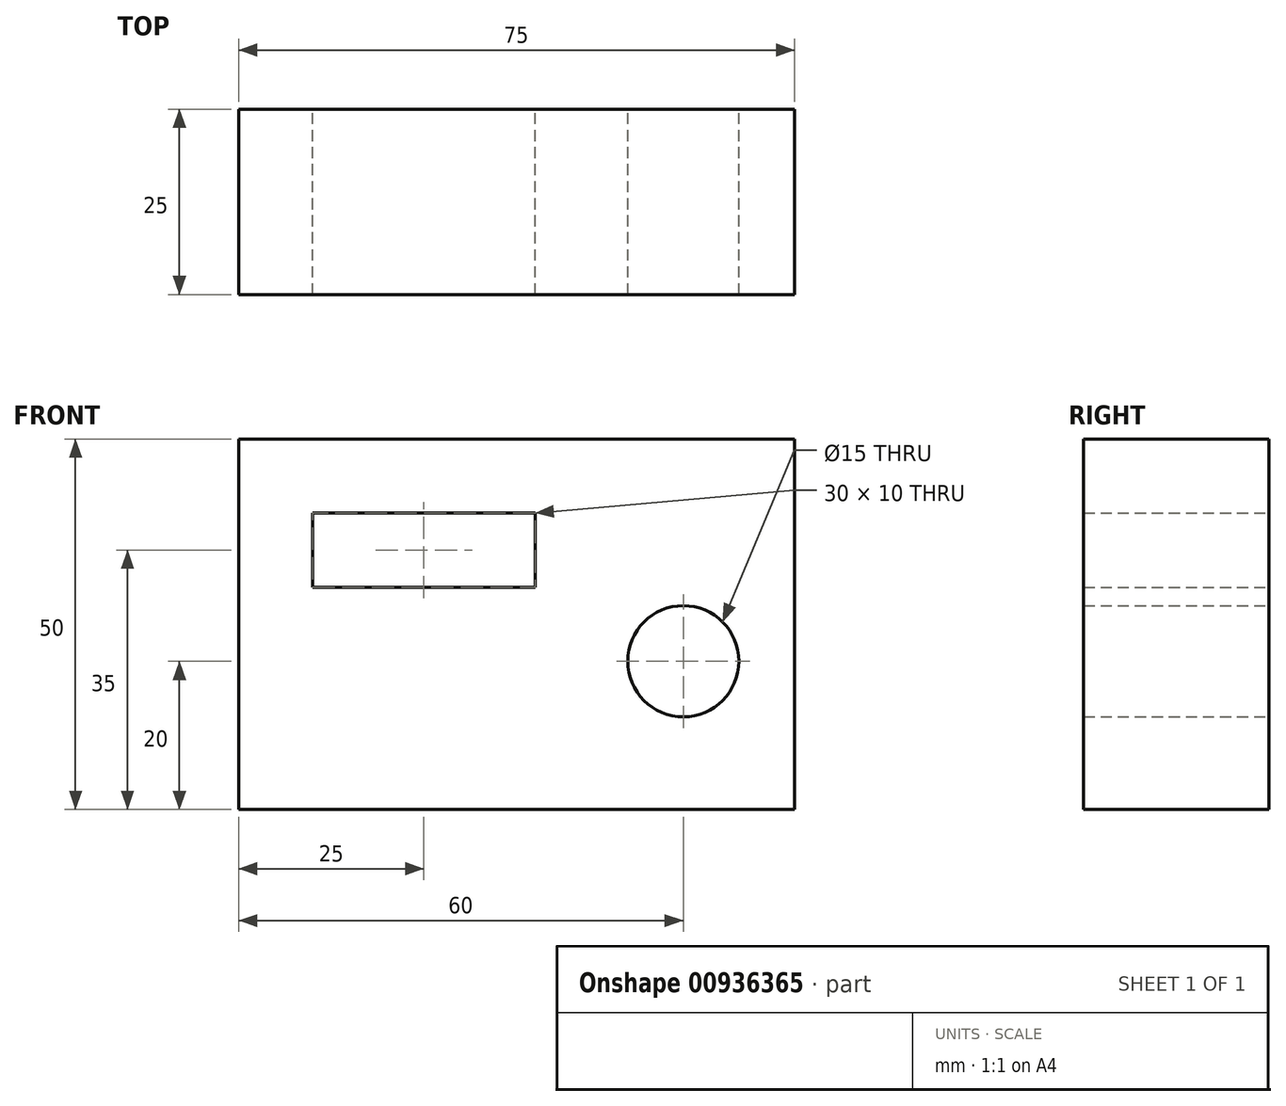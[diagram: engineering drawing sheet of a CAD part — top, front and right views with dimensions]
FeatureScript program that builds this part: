
annotation { "Feature Type Name" : "Feature", "Feature Type Description" : "" }
export const myFeature = defineFeature(function(context is Context, id is Id, definition is map)
    precondition{}
    {
        {
            var Q0;
            Q0=qCreatedBy(makeId("Front.planeOp"),FACE);
            var sketch = newSketch(context, id + "F0", { "sketchPlane" : qUnion([Q0])});
            skLineSegment(sketch, "E0.bottom", {"start": v(15, 30) * mm, "end": v(-60, 30) * mm});
            skLineSegment(sketch, "E0.top", {"start": v(15, -20) * mm, "end": v(-60, -20) * mm});
            skLineSegment(sketch, "E0.left", {"start": v(15, 30) * mm, "end": v(15, -20) * mm});
            skLineSegment(sketch, "E0.right", {"start": v(-60, 30) * mm, "end": v(-60, -20) * mm});
            skCircle(sketch, "E1", {"center": v(0, 0) * mm, "radius": 7.5 * mm});
            skLineSegment(sketch, "E2.bottom", {"start": v(-20, 10) * mm, "end": v(-50, 10) * mm});
            skLineSegment(sketch, "E2.top", {"start": v(-20, 20) * mm, "end": v(-50, 20) * mm});
            skLineSegment(sketch, "E2.left", {"start": v(-20, 10) * mm, "end": v(-20, 20) * mm});
            skLineSegment(sketch, "E2.right", {"start": v(-50, 10) * mm, "end": v(-50, 20) * mm});
            skPoint(sketch, "E2.middle", {"position": v(-35, 15) * mm});
            skSolve(sketch);
        }
        {
            var Q0;
            Q0=makeQuery(id+"F0.imprint","IMPRINT",FACE,{"disambiguationData":[TD([[makeQuery(id+"F0.imprint","IMPRINT",EDGE,{"derivedFrom":sQuery(id+"F0.wireOp",EDGE,"E0.bottom")}),1.0]])]});
            extrude(context, id + "F1", {"entities" : qUnion([Q0]), "depth" : 25 * mm, "offsetDistance" : 25 * mm});
        }
    });
